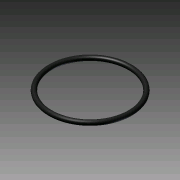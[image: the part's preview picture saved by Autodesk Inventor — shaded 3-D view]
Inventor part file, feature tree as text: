
AUTODESK INVENTOR PART (.ipt)
format: ipt  version: 2011 (Build 150239000, 239)  size: 87,552 bytes
history: native  units: in
note: dims shown in document units (in); Inventor stores cm internally (conversion verified against a paired STEP export)
features: revolve x1, sketch x1
ambient origin geometry x8: Origin, YZ Plane, XZ Plane, XY Plane, X Axis, Y Axis, Z Axis, Center Point
bodies: Solid1 (feature_tree)
feature tree (2):
  revolve  "Revolution1"  [1 undecoded]
  sketch  "Sketch1"  dims[d2=0.075in d3=0.6625in d4=90.0deg]
note: 1 required parameter value undecoded (feature->parameter linkage not recoverable at this tier; creation-order binding heuristic only, values carry confidence <= 0.55)
